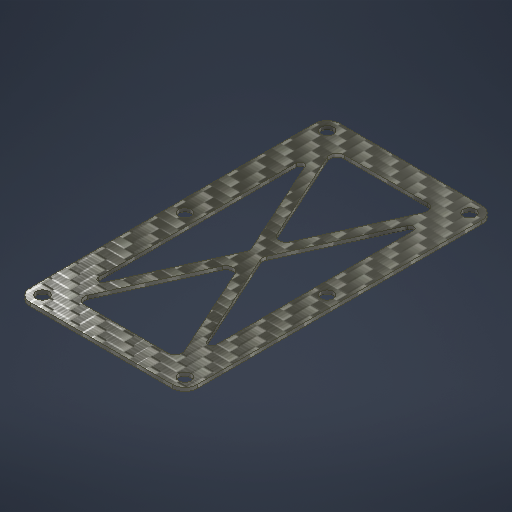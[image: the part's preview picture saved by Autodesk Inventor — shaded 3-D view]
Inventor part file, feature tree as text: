
AUTODESK INVENTOR PART (.ipt)
format: ipt  version: 2025 (Build 290162010, 162A)  size: 366,080 bytes
history: native  units: mm
features: extrude x2, fillet x2, sketch x2
ambient origin geometry x8: Origin, YZ Plane, XZ Plane, XY Plane, X Axis, Y Axis, Z Axis, Center Point
bodies: Solid1 (feature_tree)
feature tree (6):
  extrude  "Extrusion1"  Depth=80.0mm
  extrude  "Extrusion2"  Depth=3.5mm
  fillet  "Fillet1"  Radius=3.5mm
  fillet  "Fillet2"  Radius=3.5mm
  sketch  "Sketch1"  dims[d0=40.0mm d1=80.0mm]
  sketch  "Sketch2"  dims[d2=3.5mm d3=3.5mm d4=3.5mm d5=3.5mm d6=3.5mm d7=3.5mm d8=47.0mm d9=87.0mm d10=3.5mm d11=1.0mm d12=0.0mm d13=33.0mm d14=73.0mm d15=1.5mm d16=1.5mm d17=1.5mm d18=1.5mm d19=1.0mm d20=0.0mm d21=2.0mm d22=1.1mm]
